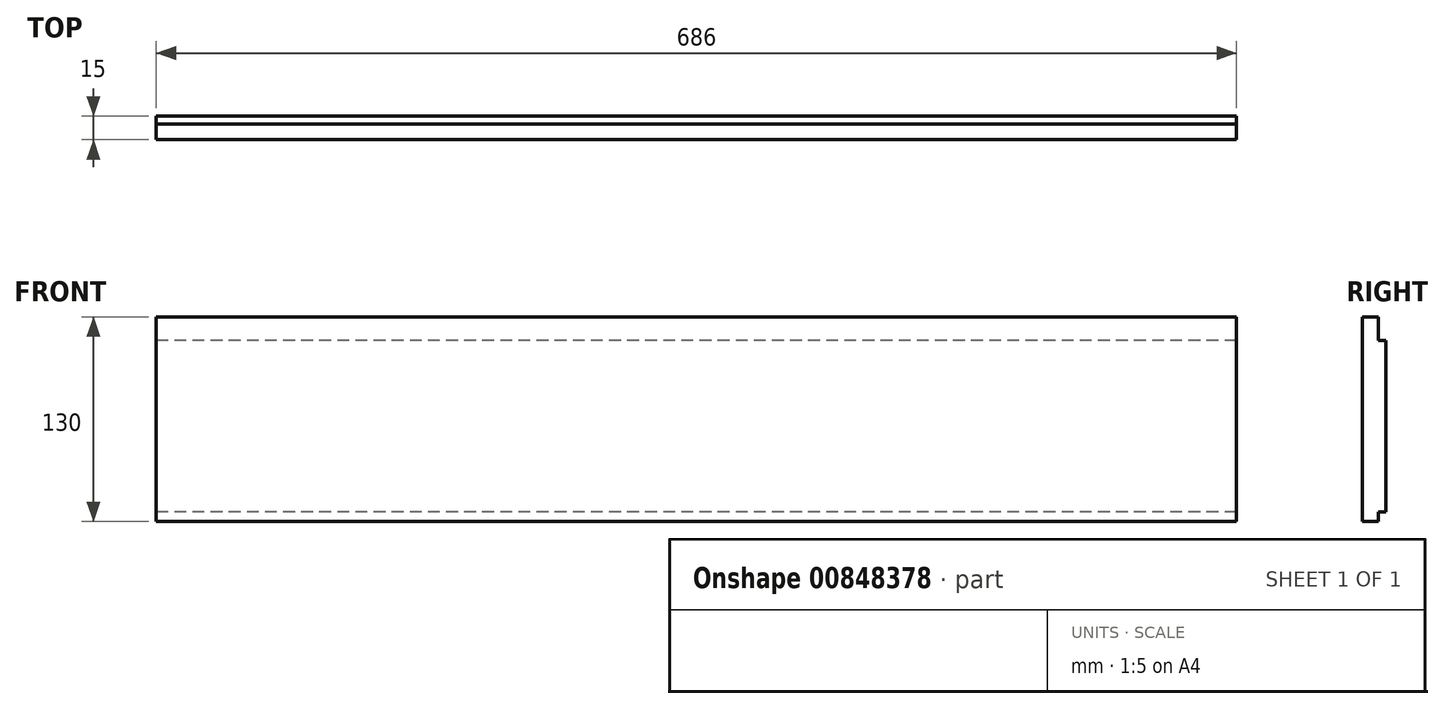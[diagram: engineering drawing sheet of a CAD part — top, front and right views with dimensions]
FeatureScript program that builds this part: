
annotation { "Feature Type Name" : "Feature", "Feature Type Description" : "" }
export const myFeature = defineFeature(function(context is Context, id is Id, definition is map)
    precondition{}
    {
        {
            var Q0;
            Q0=qCreatedBy(makeId("Top.planeOp"),FACE);
            var sketch = newSketch(context, id + "F0", { "sketchPlane" : qUnion([Q0])});
            skLineSegment(sketch, "E0.bottom", {"start": v(-343, -7.5) * mm, "end": v(343, -7.5) * mm});
            skLineSegment(sketch, "E0.top", {"start": v(-343, 7.5) * mm, "end": v(343, 7.5) * mm});
            skLineSegment(sketch, "E0.left", {"start": v(-343, -7.5) * mm, "end": v(-343, 7.5) * mm});
            skLineSegment(sketch, "E0.right", {"start": v(343, -7.5) * mm, "end": v(343, 7.5) * mm});
            skSolve(sketch);
        }
        {
            var Q0;
            Q0=qSketchRegion(id+"F0",true);
            extrude(context, id + "F1", {"entities" : qUnion([Q0]), "endBound" : BoundingType.SYMMETRIC, "depth" : 130 * mm, "offsetDistance" : 25 * mm});
        }
        {
            var Q0;
            Q0=makeQuery(id+"F1.opExtrude","SWEPT_FACE",FACE,{"disambiguationData":[OSD([sQuery(id+"F0.wireOp",EDGE,"E0.top")])]});
            var sketch = newSketch(context, id + "F2", { "sketchPlane" : qUnion([Q0])});
            skLineSegment(sketch, "E1.bottom", {"start": v(-343, 65) * mm, "end": v(343, 65) * mm});
            skLineSegment(sketch, "E1.top", {"start": v(-343, 49.8) * mm, "end": v(343, 49.8) * mm});
            skLineSegment(sketch, "E1.left", {"start": v(-343, 65) * mm, "end": v(-343, 49.8) * mm});
            skLineSegment(sketch, "E1.right", {"start": v(343, 65) * mm, "end": v(343, 49.8) * mm});
            skLineSegment(sketch, "E2.bottom", {"start": v(-343, -65) * mm, "end": v(343, -65) * mm});
            skLineSegment(sketch, "E2.top", {"start": v(-343, -58.8) * mm, "end": v(343, -58.8) * mm});
            skLineSegment(sketch, "E2.left", {"start": v(-343, -65) * mm, "end": v(-343, -58.8) * mm});
            skLineSegment(sketch, "E2.right", {"start": v(343, -65) * mm, "end": v(343, -58.8) * mm});
            skSolve(sketch);
        }
        {
            var Q0;
            Q0=qSketchRegion(id+"F2",true);
            extrude(context, id + "F3", {"entities" : qUnion([Q0]), "operationType" : NewBodyOperationType.REMOVE, "oppositeDirection" : true, "depth" : 5 * mm, "offsetDistance" : 25 * mm});
        }
        {
            var Q0;
            Q0=qCreatedBy(makeId("Front.planeOp"),FACE);
            cPlane(context, id + "F4", {"entities" : qUnion([Q0]), "cplaneType" : CPlaneType.OFFSET, "offset" : 25 * mm, "oppositeDirection" : true, "width" : 150 * mm, "height" : 150 * mm});
        }
    });
